# Revit family: 8310rdf16
name_source: partatom
category: Plumbing Fixtures
revit_build: Autodesk Revit Architecture 2012 (Build: 20110309_2315(x64)
units: mm (PartAtom-declared; Revit-internal decimal feet)

## types (1)
- 8310rdf16
    ADA Compliant = Yes
    Assembly Code = D2010400
    Base = <By Category>
    Base Length = 10.5"
    Base Width = 2.375"
    CWFU = 1
    Cold Water Connection Diameter = 1"
    Default Elevation = 48"
    Description = Two-Handle Lavatory Faucet with Spout
    Documentation Link = http://www.moen.com
    Domestic Water Flow Rate = 2.2 GPM
    Drain Type = None
    Faucet Spout Height = 7.5"
    Faucet Spout Reach = 8"
    Gooseneck Spout = <By Category>
    HWFU = 1
    Handle Type = 4" Wrist blade handles with hot and cold color indicators
    Height = 12.5"
    Hot Water Connection Diameter = 1"
    Keynote = 15410
    Length = 9.5"
    Manufacturer = Moen
    Model = 8310rdf16
    Tapered Stand alone service connection = <By Category>
    URL = www.moencommercial.com
    Vent Connection = No
    WFU = 0
    Waste Connection = No
    Width = 15.75"
    Wrist Blade Handle = <By Category>

## geometry (parser evidence)
native form markers: Sweep x1
no freeform markers — native parametric forms only
